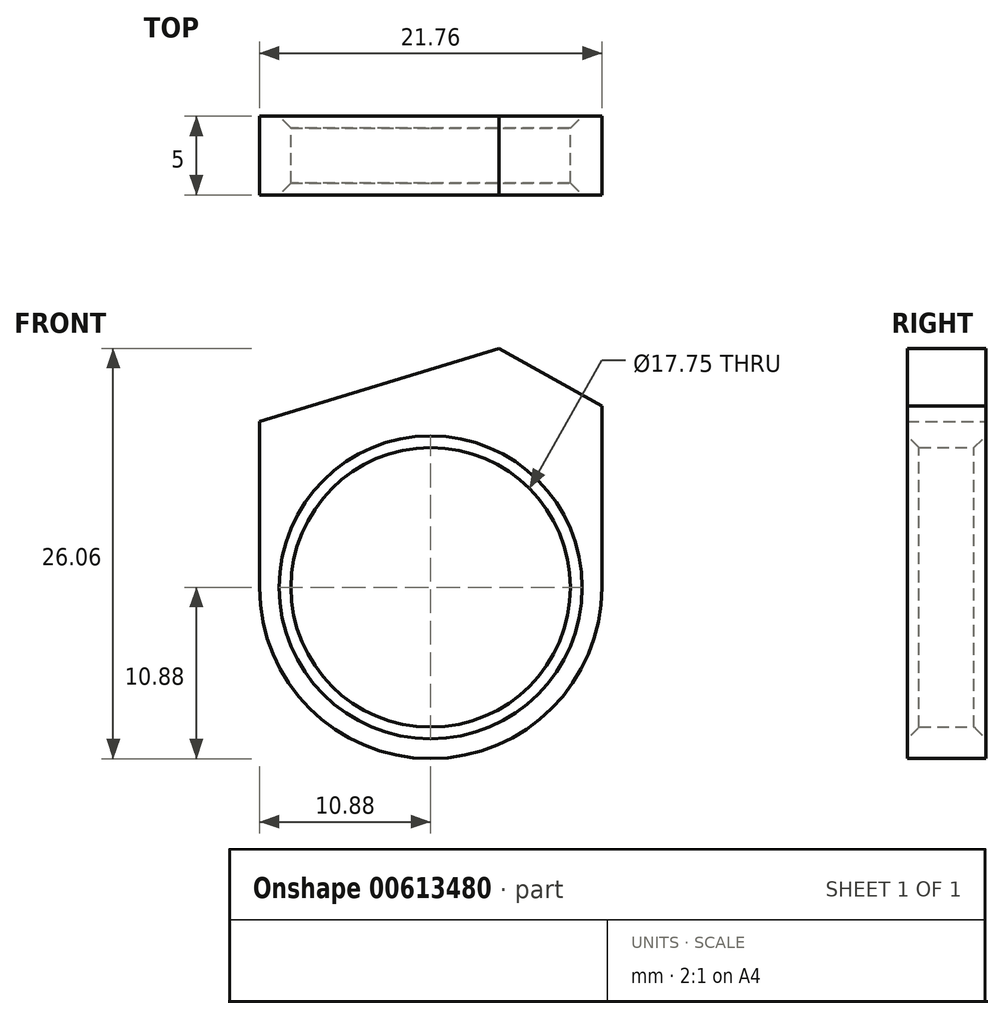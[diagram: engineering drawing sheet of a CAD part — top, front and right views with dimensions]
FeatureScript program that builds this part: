
annotation { "Feature Type Name" : "Feature", "Feature Type Description" : "" }
export const myFeature = defineFeature(function(context is Context, id is Id, definition is map)
    precondition{}
    {
        {
            var Q0;
            Q0=qCreatedBy(makeId("Front.planeOp"),FACE);
            var sketch = newSketch(context, id + "F0", { "sketchPlane" : qUnion([Q0])});
            skCircle(sketch, "E0", {"center": v(0, 0) * mm, "radius": 8.88 * mm});
            skCircle(sketch, "E1.0", {"center": v(0, 0) * mm, "radius": 10.88 * mm});
            skLineSegment(sketch, "E2", {"start": v(-10.88, 10.55) * mm, "end": v(4.34, 15.18) * mm});
            skLineSegment(sketch, "E3", {"start": v(4.34, 15.18) * mm, "end": v(10.88, 11.54) * mm});
            skLineSegment(sketch, "E4", {"start": v(-10.88, 0) * mm, "end": v(-10.88, 10.55) * mm});
            skLineSegment(sketch, "E5", {"start": v(10.88, 0) * mm, "end": v(10.88, 11.54) * mm});
            skSolve(sketch);
        }
        {
            var Q0;
            Q0=makeQuery(id+"F0.imprint","IMPRINT",FACE,{"disambiguationData":[TD([[makeQuery(id+"F0.imprint","IMPRINT",EDGE,{"derivedFrom":sQuery(id+"F0.wireOp",EDGE,"E0")}),-1.0]])]});
            var Q1;
            Q1=makeQuery(id+"F0.imprint","IMPRINT",FACE,{"disambiguationData":[TD([[makeQuery(id+"F0.imprint","IMPRINT",EDGE,{"derivedFrom":sQuery(id+"F0.wireOp",EDGE,"E2")}),-1.0]])]});
            extrude(context, id + "F1", {"entities" : qUnion([Q0, Q1]), "depth" : 2.5 * mm, "offsetDistance" : 25 * mm, "hasSecondDirection" : true, "secondDirectionOppositeDirection" : true, "secondDirectionDepth" : 2.5 * mm});
        }
        {
            var Q0;
            Q0=makeQuery(id+"F1.opExtrude","CAP_EDGE",EDGE,{"disambiguationData":[OSD([sQuery(id+"F0.wireOp",EDGE,"E0")])],"isStart":false});
            var Q1;
            Q1=makeQuery(id+"F1.opExtrude","CAP_EDGE",EDGE,{"disambiguationData":[OSD([sQuery(id+"F0.wireOp",EDGE,"E0")])],"isStart":true});
            chamfer(context, id + "F2", {"entities" : qUnion([Q0, Q1]), "width" : .75 * mm, "tangentPropagation" : true});
        }
    });
